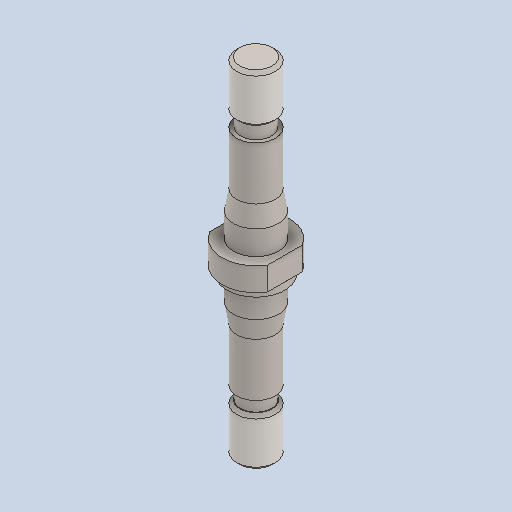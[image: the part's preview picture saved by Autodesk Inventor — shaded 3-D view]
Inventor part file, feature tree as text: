
AUTODESK INVENTOR PART (.ipt)
format: ipt  version: 2024.1 (Build 281209000, 209)  size: 129,024 bytes
history: native  units: in
note: dims shown in document units (in); Inventor stores cm internally (conversion verified against a paired STEP export)
features: chamfer x1
ambient origin geometry x8: Origin, YZ Plane, XZ Plane, XY Plane, X Axis, Y Axis, Z Axis, Center Point
bodies: Solid1 (feature_tree)
feature tree (1):
  chamfer  "Chamfer1"  [1 undecoded]
note: 1 required parameter value undecoded (feature->parameter linkage not recoverable at this tier; creation-order binding heuristic only, values carry confidence <= 0.55)
